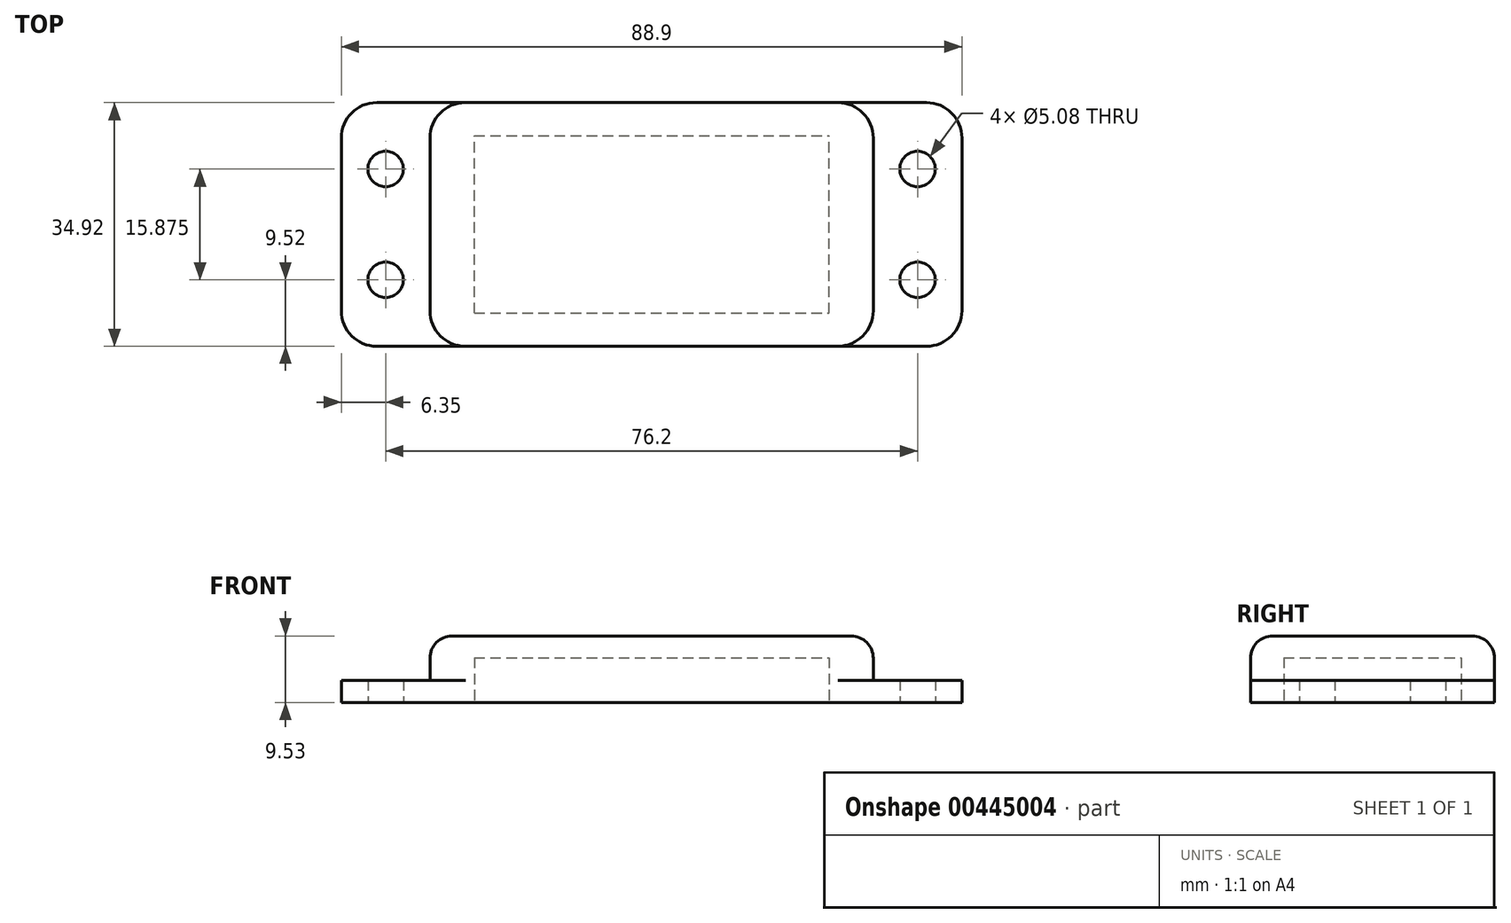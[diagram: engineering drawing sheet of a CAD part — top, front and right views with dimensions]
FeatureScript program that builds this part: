
annotation { "Feature Type Name" : "Feature", "Feature Type Description" : "" }
export const myFeature = defineFeature(function(context is Context, id is Id, definition is map)
    precondition{}
    {
        {
            var Q0;
            Q0=qCreatedBy(makeId("Front.planeOp"),FACE);
            var sketch = newSketch(context, id + "F0", { "sketchPlane" : qUnion([Q0])});
            skLineSegment(sketch, "E0.bottom", {"start": v(0, 0) * mm, "end": v(12.7, 0) * mm});
            skLineSegment(sketch, "E1", {"start": v(44.45, 3.18) * mm, "end": v(44.45, 0) * mm});
            skLineSegment(sketch, "E2", {"start": v(44.45, 0) * mm, "end": v(12.7, 0) * mm});
            skPoint(sketch, "E0.left.end.orphan", {"position": v(-31.75, 9.52) * mm});
            skPoint(sketch, "E0.left.start.orphan", {"position": v(-12.7, 0) * mm});
            skLineSegment(sketch, "E3.MirrorCS", {"start": v(-44.45, 3.18) * mm, "end": v(-44.45, 0) * mm});
            skLineSegment(sketch, "E4.MirrorCS", {"start": v(-44.45, 0) * mm, "end": v(-12.7, 0) * mm});
            skLineSegment(sketch, "E5.MirrorCS", {"start": v(0, 0) * mm, "end": v(-12.7, 0) * mm});
            skLineSegment(sketch, "E6", {"start": v(44.45, 3.18) * mm, "end": v(31.75, 3.18) * mm});
            skLineSegment(sketch, "E7", {"start": v(31.75, 3.18) * mm, "end": v(31.75, 9.53) * mm});
            skLineSegment(sketch, "E8", {"start": v(-31.75, 9.52) * mm, "end": v(-31.75, 3.18) * mm});
            skLineSegment(sketch, "E9", {"start": v(-31.75, 3.17) * mm, "end": v(-44.45, 3.17) * mm});
            skLineSegment(sketch, "E10", {"start": v(-31.75, 9.52) * mm, "end": v(31.75, 9.53) * mm});
            skSolve(sketch);
        }
        {
            var Q0;
            Q0=makeQuery(id+"F0.imprint","IMPRINT",FACE,{"disambiguationData":[TD([[makeQuery(id+"F0.imprint","IMPRINT",EDGE,{"derivedFrom":sQuery(id+"F0.wireOp",EDGE,"E0.bottom")}),1.0]])]});
            extrude(context, id + "F1", {"entities" : qUnion([Q0]), "depth" : 34.92 * mm});
        }
        {
            var Q0;
            Q0=makeQuery(id+"F1.opExtrude","SWEPT_FACE",FACE,{"disambiguationData":[OSD([sQuery(id+"F0.wireOp",EDGE,"E0.bottom"),sQuery(id+"F0.wireOp",EDGE,"E2"),sQuery(id+"F0.wireOp",EDGE,"E4.MirrorCS"),sQuery(id+"F0.wireOp",EDGE,"E5.MirrorCS")])]});
            var sketch = newSketch(context, id + "F2", { "sketchPlane" : qUnion([Q0])});
            skCircle(sketch, "E11", {"center": v(-38.1, 25.4) * mm, "radius": 2.54 * mm});
            skLineSegment(sketch, "E12", {"start": v(44.45, 17.46) * mm, "end": v(23.29, 17.46) * mm});
            skCircle(sketch, "E13.MirrorC", {"center": v(-38.1, 9.52) * mm, "radius": 2.54 * mm});
            skCircle(sketch, "E14.MirrorC", {"center": v(38.1, 25.4) * mm, "radius": 2.54 * mm});
            skCircle(sketch, "E15.MirrorC", {"center": v(38.1, 9.52) * mm, "radius": 2.54 * mm});
            skSolve(sketch);
        }
        {
            var Q0;
            Q0 = qSketchRegion(id + "F2", true);
            extrude(context, id + "F3", {"entities" : qUnion([Q0]), "operationType" : NewBodyOperationType.REMOVE, "oppositeDirection" : true, "depth" : 25.4 * mm});
        }
        {
            var Q0;
            Q0=makeQuery(id+"F1.opExtrude","CAP_EDGE",EDGE,{"disambiguationData":[OSD([sQuery(id+"F0.wireOp",EDGE,"E3.MirrorCS")])],"isStart":false});
            var Q1;
            Q1=makeQuery(id+"F1.opExtrude","CAP_EDGE",EDGE,{"disambiguationData":[OSD([sQuery(id+"F0.wireOp",EDGE,"E1")])],"isStart":false});
            var Q2;
            Q2=makeQuery(id+"F1.opExtrude","CAP_EDGE",EDGE,{"disambiguationData":[OSD([sQuery(id+"F0.wireOp",EDGE,"E1")])],"isStart":true});
            var Q3;
            Q3=makeQuery(id+"F1.opExtrude","CAP_EDGE",EDGE,{"disambiguationData":[OSD([sQuery(id+"F0.wireOp",EDGE,"E3.MirrorCS")])],"isStart":true});
            var Q4;
            Q4=makeQuery(id+"F1.opExtrude","CAP_EDGE",EDGE,{"disambiguationData":[OSD([sQuery(id+"F0.wireOp",EDGE,"E7")])],"isStart":true});
            var Q5;
            Q5=makeQuery(id+"F1.opExtrude","CAP_EDGE",EDGE,{"disambiguationData":[OSD([sQuery(id+"F0.wireOp",EDGE,"E8")])],"isStart":true});
            var Q6;
            Q6=makeQuery(id+"F1.opExtrude","CAP_EDGE",EDGE,{"disambiguationData":[OSD([sQuery(id+"F0.wireOp",EDGE,"E7")])],"isStart":false});
            var Q7;
            Q7=makeQuery(id+"F1.opExtrude","CAP_EDGE",EDGE,{"disambiguationData":[OSD([sQuery(id+"F0.wireOp",EDGE,"E8")])],"isStart":false});
            fillet(context, id + "F4", {"entities" : qUnion([Q0, Q1, Q2, Q3, Q4, Q5, Q6, Q7]), "radius" : 5.08 * mm, "tangentPropagation" : true, "allowEdgeOverflow" : false});
        }
        {
            var Q0;
            Q0=makeQuery(id+"F4.opFillet","BLEND_EDGE",EDGE,{"blendedFrom":[makeQuery(id+"F1.opExtrude","CAP_EDGE",EDGE,{"disambiguationData":[OSD([sQuery(id+"F0.wireOp",EDGE,"E8")])],"isStart":false}),makeQuery(id+"F1.opExtrude","SWEPT_FACE",FACE,{"disambiguationData":[OSD([sQuery(id+"F0.wireOp",EDGE,"E10")])]})],"blendedInto":[makeQuery(id+"F1.opExtrude","SWEPT_FACE",FACE,{"disambiguationData":[OSD([sQuery(id+"F0.wireOp",EDGE,"E10")])]})]});
            fillet(context, id + "F5", {"entities" : qUnion([Q0]), "radius" : 3.17 * mm, "tangentPropagation" : true, "allowEdgeOverflow" : false});
        }
        {
            var Q0;
            Q0=makeQuery(id+"F1.opExtrude","SWEPT_FACE",FACE,{"disambiguationData":[OSD([sQuery(id+"F0.wireOp",EDGE,"E0.bottom"),sQuery(id+"F0.wireOp",EDGE,"E2"),sQuery(id+"F0.wireOp",EDGE,"E4.MirrorCS"),sQuery(id+"F0.wireOp",EDGE,"E5.MirrorCS")])]});
            var sketch = newSketch(context, id + "F6", { "sketchPlane" : qUnion([Q0])});
            skLineSegment(sketch, "E16.bottom", {"start": v(-25.4, 30.16) * mm, "end": v(25.4, 30.16) * mm});
            skLineSegment(sketch, "E16.top", {"start": v(-25.4, 4.76) * mm, "end": v(25.4, 4.76) * mm});
            skLineSegment(sketch, "E16.left", {"start": v(-25.4, 30.16) * mm, "end": v(-25.4, 4.76) * mm});
            skLineSegment(sketch, "E16.right", {"start": v(25.4, 30.16) * mm, "end": v(25.4, 4.76) * mm});
            skSolve(sketch);
        }
        {
            var Q0;
            Q0 = qSketchRegion(id + "F6", true);
            extrude(context, id + "F7", {"entities" : qUnion([Q0]), "operationType" : NewBodyOperationType.REMOVE, "oppositeDirection" : true, "depth" : 6.4 * mm});
        }
    });
